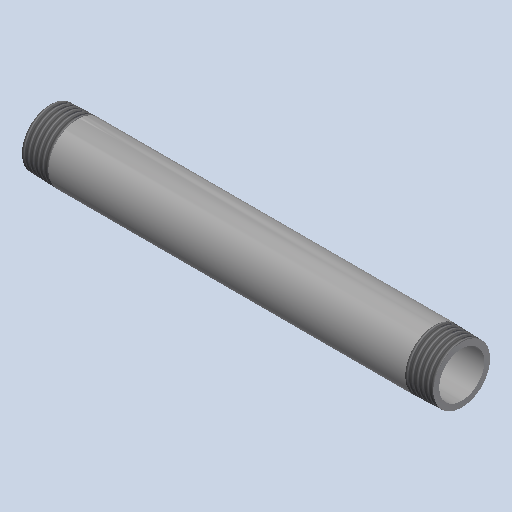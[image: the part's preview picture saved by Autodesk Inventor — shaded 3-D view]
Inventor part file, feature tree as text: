
AUTODESK INVENTOR PART (.ipt)
format: ipt  version: 2025 (Build 290162000, 162)  size: 196,096 bytes
history: native  units: mm (DEFAULTED — no unit token found)
features: other x8, revolve x1
ambient origin geometry x8: Origin, YZ Plane, XZ Plane, XY Plane, X Axis, Y Axis, Z Axis, Center Point
bodies: Solid1 (feature_tree)
feature tree (9):
  revolve  "Revolution1"  [1 undecoded]
  other  "Work Axis1"
  other  "Work Point5"
  other  "Work Axis2"
  other  "Work Point6"
  other  "Work Axis3"
  other  "Work Axis4"
  other  "Work Point7"
  other  "Work Point8"
note: 1 required parameter value undecoded (feature->parameter linkage not recoverable at this tier; creation-order binding heuristic only, values carry confidence <= 0.55)
